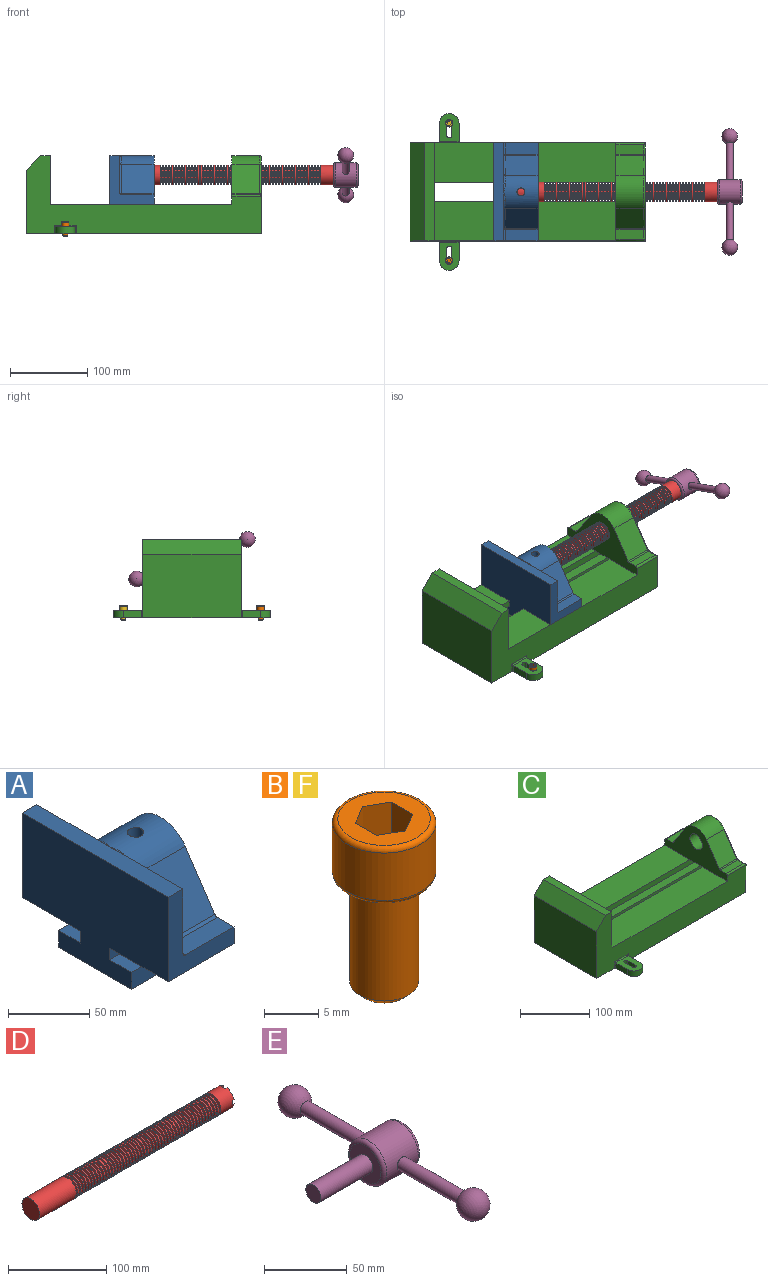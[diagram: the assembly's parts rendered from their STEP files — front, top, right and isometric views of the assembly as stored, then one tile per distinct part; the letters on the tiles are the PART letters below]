
ASSEMBLY  parts=6 mates=6
PART A: 36 faces, bbox 57.2x127x89 mm
  f0: plane 57.15x50.8mm, normal (0,0,-1), area 2903.2mm2, adj f6,f9,f10,f23
  f1: cylinder r=12.7mm len=44.45mm, axis (1,0,0), area 3464.3mm2, adj f6,f15,f16
  f2: plane 41.91x14.52mm, normal (0,0,1), area 608.5mm2, adj f6,f11,f24,f25
  f3: plane 51.86x48.26mm, normal (1,0,0), area 1495.7mm2, adj f8,f10,f31,f33,f35
  f4: plane 51.86x48.26mm, normal (1,0,0), area 1495.7mm2, adj f8,f11,f24,f28,f29
  f5: plane 57.15x50.8mm, normal (0,0,-1), area 2903.2mm2, adj f6,f9,f11,f22
  f6: plane 127x85.09mm, normal (1,0,0), area 5190.6mm2, adj f0,f1,f2,f5,f7,f10,f11,f12
  f7: plane 41.91x14.52mm, normal (0,0,1), area 608.5mm2, adj f6,f10,f30,f31
  f8: plane 127x12.7mm, normal (0,0,1), area 1612.9mm2, adj f3,f4,f9,f10,f11,f26,f34
  f9: plane 127x85.09mm, normal (-1,0,0), area 9096.8mm2, adj f0,f5,f8,f10,f11,f17,f18,f19
  f10: plane 63.5x57.15mm, normal (0,-1,0), area 1372.3mm2, adj f0,f3,f6,f7,f8,f9,f31
  f11: plane 63.5x57.15mm, normal (0,1,0), area 1372.3mm2, adj f2,f4,f5,f6,f8,f9,f24
  f12: plane 41.91x38.43mm, normal (0,-0.83,0.56), area 1939.2mm2, adj f6,f13,f30,f33
  f13: cylinder r=25.4mm len=44.45mm, axis (1,0,0), area 2026.5mm2, adj f6,f12,f14,f16,f26,f28,f34,f35
  f14: plane 41.91x38.43mm, normal (0,0.83,0.56), area 1939.2mm2, adj f6,f13,f25,f29
  f15: plane 25.4x25.4mm, normal (1,0,0), area 506.7mm2, adj f1
  f16: cylinder r=5.08mm len=13.76mm, axis (0,0,1), area 414mm2, adj f1,f13
  f17: plane 57.15x19.05mm, normal (0,0,1), area 1088.7mm2, adj f6,f9,f18,f23
  f18: plane 57.15x12.7mm, normal (0,-1,0), area 725.8mm2, adj f6,f9,f17,f19
  f19: plane 63.5x57.15mm, normal (0,0,-1), area 3629mm2, adj f6,f9,f18,f20
  f20: plane 57.15x12.7mm, normal (0,1,0), area 725.8mm2, adj f6,f9,f19,f21
  f21: plane 57.15x19.05mm, normal (0,0,1), area 1088.7mm2, adj f6,f9,f20,f22
  f22: plane 57.15x8.89mm, normal (0,1,0), area 508.1mm2, adj f5,f6,f9,f21
  f23: plane 57.15x8.89mm, normal (0,-1,0), area 508.1mm2, adj f0,f6,f9,f17
  f24: cylinder r=2.54mm len=14.52mm, axis (0,-1,0), area 57.9mm2, adj f2,f4,f11,f27
  f25: cylinder r=2.54mm len=41.91mm, axis (1,0,0), area 104.3mm2, adj f2,f6,f14,f27
  f26: bspline ~12.24x2.8mm, area 20.9mm2, adj f8,f13,f28
  f27: sphere r=2.54mm, area 6.3mm2, adj f24,f25,f29
  f28: torus R=27.94mm, axis (1,0,0), area 57.8mm2, adj f4,f13,f26,f29
  f29: cylinder r=2.54mm len=39.84mm, axis (0,-0.56,0.83), area 184.6mm2, adj f4,f14,f27,f28
  f30: cylinder r=2.54mm len=41.91mm, axis (1,0,0), area 104.3mm2, adj f6,f7,f12,f32
  f31: cylinder r=2.54mm len=14.52mm, axis (0,-1,0), area 57.9mm2, adj f3,f7,f10,f32
  f32: sphere r=2.54mm, area 6.3mm2, adj f30,f31,f33
  f33: cylinder r=2.54mm len=39.84mm, axis (0,-0.56,-0.83), area 184.6mm2, adj f3,f12,f32,f35
  f34: bspline ~12.24x2.8mm, area 20.9mm2, adj f8,f13,f35
  f35: torus R=27.94mm, axis (1,0,0), area 57.8mm2, adj f3,f13,f33,f34
PART B: 15 faces, bbox 10.3x10.3x19.1 mm
  f0: plane 8.51x8.51mm, normal (0,0,1), area 37.2mm2, adj f5,f6,f7,f8,f9,f10,f14
  f1: cylinder r=3.17mm len=11.94mm, axis (0,0,1), area 238.2mm2, adj f4,f12
  f2: plane 4.83x4.83mm, normal (0,0,-1), area 18.3mm2, adj f12
  f3: cylinder r=4.76mm len=9.53mm, axis (0,0,-1), area 159.6mm2, adj f13,f14
  f4: plane 8.51x8.51mm, normal (0,0,-1), area 25.2mm2, adj f1,f13
  f5: plane 4.83x2.38mm, normal (-0.5,-0.87,0), area 13.3mm2, adj f0,f6,f10,f11
  f6: plane 4.83x2.38mm, normal (0.5,-0.87,0), area 13.3mm2, adj f0,f5,f7,f11
  f7: plane 4.83x2.75mm, normal (1,0,0), area 13.3mm2, adj f0,f6,f8,f11
  f8: plane 4.83x2.38mm, normal (0.5,0.87,0), area 13.3mm2, adj f0,f7,f9,f11
  f9: plane 4.83x2.38mm, normal (-0.5,0.87,0), area 13.3mm2, adj f0,f8,f10,f11
  f10: plane 4.83x2.75mm, normal (-1,0,0), area 13.3mm2, adj f0,f5,f9,f11
  f11: plane 5.5x4.76mm, normal (0,0,1), area 19.6mm2, adj f5,f6,f7,f8,f9,f10
  f12: cone r=3.17mm half-angle=45deg, axis (0,0,1), area 18.9mm2, adj f1,f2
  f13: torus R=4.25mm, axis (0,0,1), area 23mm2, adj f3,f4
  f14: torus R=4.25mm, axis (0,0,1), area 23mm2, adj f0,f3
PART C: 61 faces, bbox 304.8x203.2x103.7 mm
  f0: plane 304.8x101.6mm, normal (0,1,0), area 13520.3mm2, adj f3,f4,f5,f6,f7,f8,f9,f16
  f1: plane 304.8x101.6mm, normal (0,-1,0), area 13520.3mm2, adj f2,f3,f5,f6,f7,f8,f9,f16
  f2: plane 234.95x50.8mm, normal (0,0,1), area 11935.5mm2, adj f1,f5,f16,f26
  f3: plane 127x99.06mm, normal (1,0,0), area 7097.5mm2, adj f0,f1,f9,f14,f17,f18,f19,f20
  f4: plane 234.95x50.8mm, normal (0,0,1), area 11935.5mm2, adj f0,f5,f16,f27
  f5: plane 127x101.6mm, normal (1,0,0), area 9516.1mm2, adj f0,f1,f2,f4,f6,f9,f18,f19
  f6: plane 127x12.7mm, normal (0,0,1), area 1612.9mm2, adj f0,f1,f5,f7
  f7: plane 127x19.05mm, normal (-0.71,0,0.71), area 3421.5mm2, adj f0,f1,f6,f8
  f8: plane 127x82.55mm, normal (-1,0,0), area 10483.8mm2, adj f0,f1,f7,f9
  f9: plane 304.8x203.2mm, normal (0,0,-1), area 33298.3mm2, adj f0,f1,f3,f5,f8,f21,f22,f39
  f10: plane 35.56x11.98mm, normal (0,0,1), area 426mm2, adj f16,f28,f29,f30
  f11: plane 38.43x35.56mm, normal (0,0.83,0.56), area 1645.4mm2, adj f12,f16,f29,f32
  f12: cylinder r=25.4mm len=42.19mm, axis (1,0,0), area 1770.2mm2, adj f11,f13,f16,f33
  f13: plane 38.43x35.56mm, normal (0,-0.83,0.56), area 1645.4mm2, adj f12,f16,f34,f35
  f14: cylinder r=12.7mm len=38.1mm, axis (1,0,0), area 3040.2mm2, adj f3,f16
  f15: plane 35.56x11.98mm, normal (0,0,1), area 426mm2, adj f16,f34,f36,f38
  f16: plane 127x63.5mm, normal (-1,0,0), area 4155.5mm2, adj f0,f1,f2,f4,f10,f11,f12,f13
  f17: plane 38.1x25.4mm, normal (0,0,-1), area 967.7mm2, adj f3,f16,f26,f27
  f18: plane 273.05x19.05mm, normal (0,0,-1), area 5201.6mm2, adj f3,f5,f19,f26
  f19: plane 273.05x12.7mm, normal (0,1,0), area 3467.7mm2, adj f3,f5,f18,f20
  f20: plane 273.05x19.05mm, normal (0,0,1), area 5201.6mm2, adj f3,f5,f19,f21
  f21: plane 273.05x16.51mm, normal (0,1,0), area 4508.1mm2, adj f3,f5,f9,f20
  f22: plane 273.05x16.51mm, normal (0,-1,0), area 4508.1mm2, adj f3,f5,f9,f23
  f23: plane 273.05x19.05mm, normal (0,0,1), area 5201.6mm2, adj f3,f5,f22,f24
  f24: plane 273.05x12.7mm, normal (0,-1,0), area 3467.7mm2, adj f3,f5,f23,f25
  f25: plane 273.05x19.05mm, normal (0,0,-1), area 5201.6mm2, adj f3,f5,f24,f27
  f26: plane 273.05x8.89mm, normal (0,1,0), area 2427.4mm2, adj f2,f3,f5,f17,f18
  f27: plane 273.05x8.89mm, normal (0,-1,0), area 2427.4mm2, adj f3,f4,f5,f17,f25
  f28: cylinder r=2.54mm len=38.1mm, axis (1,0,0), area 148.3mm2, adj f0,f10,f16,f30
  f29: cylinder r=2.54mm len=35.56mm, axis (-1,0,0), area 88.5mm2, adj f10,f11,f16,f31
  f30: cylinder r=2.54mm len=14.52mm, axis (0,1,0), area 54.3mm2, adj f3,f10,f28,f31
  f31: torus R=5.08mm, axis (-1,0,0), area 13.5mm2, adj f3,f29,f30,f32
  f32: cylinder r=2.54mm len=39.84mm, axis (0,0.56,-0.83), area 184.6mm2, adj f3,f11,f31,f33
  f33: torus R=22.86mm, axis (-1,0,0), area 191.4mm2, adj f3,f12,f32,f35
  f34: cylinder r=2.54mm len=35.56mm, axis (-1,0,0), area 88.5mm2, adj f13,f15,f16,f37
  f35: cylinder r=2.54mm len=39.84mm, axis (0,0.56,0.83), area 184.6mm2, adj f3,f13,f33,f37
  f36: cylinder r=2.54mm len=38.1mm, axis (-1,0,0), area 148.3mm2, adj f1,f15,f16,f38
  f37: torus R=5.08mm, axis (-1,0,0), area 13.5mm2, adj f3,f34,f35,f38
  f38: cylinder r=2.54mm len=14.52mm, axis (0,1,0), area 54.3mm2, adj f3,f15,f36,f37
  f39: plane 23.88x9.53mm, normal (-1,0,0), area 227.4mm2, adj f9,f45,f46,f60
  f40: plane 23.88x9.53mm, normal (1,0,0), area 227.4mm2, adj f9,f45,f46,f58
  f41: cylinder r=3.3mm len=9.53mm, axis (0,0,-1), area 98.8mm2, adj f9,f42,f44,f46
  f42: plane 15.62x9.53mm, normal (-1,0,0), area 148.8mm2, adj f9,f41,f43,f46
  f43: cylinder r=3.3mm len=9.53mm, axis (0,0,-1), area 98.8mm2, adj f9,f42,f44,f46
  f44: plane 15.62x9.53mm, normal (1,0,0), area 148.8mm2, adj f9,f41,f43,f46
  f45: cylinder r=12.7mm len=25.4mm, axis (0,0,-1), area 380mm2, adj f9,f39,f40,f46
  f46: plane 36.58x25.4mm, normal (0,0,1), area 722.4mm2, adj f39,f40,f41,f42,f43,f44,f45,f59
  f47: plane 23.88x9.53mm, normal (-1,0,0), area 227.4mm2, adj f9,f53,f54,f56
  f48: plane 23.88x9.53mm, normal (1,0,0), area 227.4mm2, adj f9,f53,f54,f55
  f49: cylinder r=3.3mm len=9.53mm, axis (0,0,-1), area 98.8mm2, adj f9,f50,f52,f54
  f50: plane 15.62x9.53mm, normal (-1,0,0), area 148.8mm2, adj f9,f49,f51,f54
  f51: cylinder r=3.3mm len=9.53mm, axis (0,0,-1), area 98.8mm2, adj f9,f50,f52,f54
  f52: plane 15.62x9.53mm, normal (1,0,0), area 148.8mm2, adj f9,f49,f51,f54
  f53: cylinder r=12.7mm len=25.4mm, axis (0,0,-1), area 380mm2, adj f9,f47,f48,f54
  f54: plane 36.58x25.4mm, normal (0,0,1), area 722.4mm2, adj f47,f48,f49,f50,f51,f52,f53,f57
  f55: cylinder r=1.52mm len=11.05mm, axis (0,0,-1), area 24.1mm2, adj f0,f9,f48,f57
  f56: cylinder r=1.52mm len=11.05mm, axis (0,0,1), area 24.1mm2, adj f0,f9,f47,f57
  f57: cylinder r=1.52mm len=28.45mm, axis (1,0,0), area 63.5mm2, adj f0,f54,f55,f56
  f58: cylinder r=1.52mm len=11.05mm, axis (0,0,1), area 24.1mm2, adj f1,f9,f40,f59
  f59: cylinder r=1.52mm len=28.45mm, axis (-1,0,0), area 63.5mm2, adj f1,f46,f58,f60
  f60: cylinder r=1.52mm len=11.05mm, axis (0,0,-1), area 24.1mm2, adj f1,f9,f39,f59
PART D: 220 faces, bbox 279.4x25.4x25.4 mm
  f0: cylinder r=12.7mm len=25.4mm, axis (-1,0,0), area 1468.2mm2, adj f1,f2,f3,f5,f7,f208,f209,f210
  f1: plane 9.9x9.9mm, normal (1,0,0), area 62.3mm2, adj f0,f4,f213,f216
  f2: plane 9.9x9.9mm, normal (1,0,0), area 62.3mm2, adj f0,f4,f210,f218
  f3: plane 9.9x9.9mm, normal (1,0,0), area 62.3mm2, adj f0,f4,f209,f212
  f4: cylinder r=6.35mm len=25.4mm, axis (1,0,0), area 960.3mm2, adj f1,f2,f3,f5,f6,f208,f209,f210
  f5: plane 9.9x9.9mm, normal (1,0,0), area 62.3mm2, adj f0,f4,f215,f217
  f6: plane 12.7x12.7mm, normal (1,0,0), area 126.7mm2, adj f4
  f7: cone r=12.7mm half-angle=76deg, axis (1,0,0), area 188mm2, adj f0,f9
  f8: cone r=10.16mm half-angle=76deg, axis (-1,0,0), area 188mm2, adj f9,f10
  f9: cylinder r=10.16mm len=20.32mm, axis (1,0,0), area 81.1mm2, adj f7,f8
  f10: cylinder r=12.7mm len=25.4mm, axis (-1,0,0), area 131.7mm2, adj f8,f11
  f11: cone r=12.7mm half-angle=76deg, axis (1,0,0), area 188mm2, adj f10,f13
  f12: cone r=10.16mm half-angle=76deg, axis (-1,0,0), area 188mm2, adj f13,f14
  f13: cylinder r=10.16mm len=20.32mm, axis (1,0,0), area 81.1mm2, adj f11,f12
  f14: cylinder r=12.7mm len=25.4mm, axis (-1,0,0), area 131.7mm2, adj f12,f15
  f15: cone r=12.7mm half-angle=76deg, axis (1,0,0), area 188mm2, adj f14,f17
  f16: cone r=10.16mm half-angle=76deg, axis (-1,0,0), area 188mm2, adj f17,f18
  f17: cylinder r=10.16mm len=20.32mm, axis (1,0,0), area 81.1mm2, adj f15,f16
  f18: cylinder r=12.7mm len=25.4mm, axis (-1,0,0), area 131.7mm2, adj f16,f19
  f19: cone r=12.7mm half-angle=76deg, axis (1,0,0), area 188mm2, adj f18,f21
  f20: cone r=10.16mm half-angle=76deg, axis (-1,0,0), area 188mm2, adj f21,f22
  f21: cylinder r=10.16mm len=20.32mm, axis (1,0,0), area 81.1mm2, adj f19,f20
  f22: cylinder r=12.7mm len=25.4mm, axis (-1,0,0), area 131.7mm2, adj f20,f23
  f23: cone r=12.7mm half-angle=76deg, axis (1,0,0), area 188mm2, adj f22,f25
  f24: cone r=10.16mm half-angle=76deg, axis (-1,0,0), area 188mm2, adj f25,f26
  f25: cylinder r=10.16mm len=20.32mm, axis (1,0,0), area 81.1mm2, adj f23,f24
  f26: cylinder r=12.7mm len=25.4mm, axis (-1,0,0), area 131.7mm2, adj f24,f27
  f27: cone r=12.7mm half-angle=76deg, axis (1,0,0), area 188mm2, adj f26,f29
  f28: cone r=10.16mm half-angle=76deg, axis (-1,0,0), area 188mm2, adj f29,f30
  f29: cylinder r=10.16mm len=20.32mm, axis (1,0,0), area 81.1mm2, adj f27,f28
  f30: cylinder r=12.7mm len=25.4mm, axis (-1,0,0), area 131.7mm2, adj f28,f31
  f31: cone r=12.7mm half-angle=76deg, axis (1,0,0), area 188mm2, adj f30,f33
  f32: cone r=10.16mm half-angle=76deg, axis (-1,0,0), area 188mm2, adj f33,f34
  f33: cylinder r=10.16mm len=20.32mm, axis (1,0,0), area 81.1mm2, adj f31,f32
  f34: cylinder r=12.7mm len=25.4mm, axis (-1,0,0), area 131.7mm2, adj f32,f35
  f35: cone r=12.7mm half-angle=76deg, axis (1,0,0), area 188mm2, adj f34,f37
  f36: cone r=10.16mm half-angle=76deg, axis (-1,0,0), area 188mm2, adj f37,f38
  f37: cylinder r=10.16mm len=20.32mm, axis (1,0,0), area 81.1mm2, adj f35,f36
  f38: cylinder r=12.7mm len=25.4mm, axis (-1,0,0), area 131.7mm2, adj f36,f39
  f39: cone r=12.7mm half-angle=76deg, axis (1,0,0), area 188mm2, adj f38,f41
  f40: cone r=10.16mm half-angle=76deg, axis (-1,0,0), area 188mm2, adj f41,f42
  f41: cylinder r=10.16mm len=20.32mm, axis (1,0,0), area 81.1mm2, adj f39,f40
  f42: cylinder r=12.7mm len=25.4mm, axis (-1,0,0), area 131.7mm2, adj f40,f43
  f43: cone r=12.7mm half-angle=76deg, axis (1,0,0), area 188mm2, adj f42,f45
  f44: cone r=10.16mm half-angle=76deg, axis (-1,0,0), area 188mm2, adj f45,f46
  f45: cylinder r=10.16mm len=20.32mm, axis (1,0,0), area 81.1mm2, adj f43,f44
  f46: cylinder r=12.7mm len=25.4mm, axis (-1,0,0), area 131.7mm2, adj f44,f47
  f47: cone r=12.7mm half-angle=76deg, axis (1,0,0), area 188mm2, adj f46,f49
  f48: cone r=10.16mm half-angle=76deg, axis (-1,0,0), area 188mm2, adj f49,f50
  f49: cylinder r=10.16mm len=20.32mm, axis (1,0,0), area 81.1mm2, adj f47,f48
  f50: cylinder r=12.7mm len=25.4mm, axis (-1,0,0), area 131.7mm2, adj f48,f51
  f51: cone r=12.7mm half-angle=76deg, axis (1,0,0), area 188mm2, adj f50,f53
  f52: cone r=10.16mm half-angle=76deg, axis (-1,0,0), area 188mm2, adj f53,f54
  f53: cylinder r=10.16mm len=20.32mm, axis (1,0,0), area 81.1mm2, adj f51,f52
  f54: cylinder r=12.7mm len=25.4mm, axis (-1,0,0), area 131.7mm2, adj f52,f55
  f55: cone r=12.7mm half-angle=76deg, axis (1,0,0), area 188mm2, adj f54,f57
  f56: cone r=10.16mm half-angle=76deg, axis (-1,0,0), area 188mm2, adj f57,f58
  f57: cylinder r=10.16mm len=20.32mm, axis (1,0,0), area 81.1mm2, adj f55,f56
  f58: cylinder r=12.7mm len=25.4mm, axis (-1,0,0), area 131.7mm2, adj f56,f59
  f59: cone r=12.7mm half-angle=76deg, axis (1,0,0), area 188mm2, adj f58,f61
  f60: cone r=10.16mm half-angle=76deg, axis (-1,0,0), area 188mm2, adj f61,f62
  f61: cylinder r=10.16mm len=20.32mm, axis (1,0,0), area 81.1mm2, adj f59,f60
  f62: cylinder r=12.7mm len=25.4mm, axis (-1,0,0), area 131.7mm2, adj f60,f63
  f63: cone r=12.7mm half-angle=76deg, axis (1,0,0), area 188mm2, adj f62,f65
  f64: cone r=10.16mm half-angle=76deg, axis (-1,0,0), area 188mm2, adj f65,f66
  f65: cylinder r=10.16mm len=20.32mm, axis (1,0,0), area 81.1mm2, adj f63,f64
  f66: cylinder r=12.7mm len=25.4mm, axis (-1,0,0), area 131.7mm2, adj f64,f67
  f67: cone r=12.7mm half-angle=76deg, axis (1,0,0), area 188mm2, adj f66,f69
  f68: cone r=10.16mm half-angle=76deg, axis (-1,0,0), area 188mm2, adj f69,f70
  f69: cylinder r=10.16mm len=20.32mm, axis (1,0,0), area 81.1mm2, adj f67,f68
  f70: cylinder r=12.7mm len=25.4mm, axis (-1,0,0), area 131.7mm2, adj f68,f71
  f71: cone r=12.7mm half-angle=76deg, axis (1,0,0), area 188mm2, adj f70,f73
  f72: cone r=10.16mm half-angle=76deg, axis (-1,0,0), area 188mm2, adj f73,f74
  f73: cylinder r=10.16mm len=20.32mm, axis (1,0,0), area 81.1mm2, adj f71,f72
  f74: cylinder r=12.7mm len=25.4mm, axis (-1,0,0), area 131.7mm2, adj f72,f75
  f75: cone r=12.7mm half-angle=76deg, axis (1,0,0), area 188mm2, adj f74,f77
  f76: cone r=10.16mm half-angle=76deg, axis (-1,0,0), area 188mm2, adj f77,f78
  f77: cylinder r=10.16mm len=20.32mm, axis (1,0,0), area 81.1mm2, adj f75,f76
  f78: cylinder r=12.7mm len=25.4mm, axis (-1,0,0), area 131.7mm2, adj f76,f79
  f79: cone r=12.7mm half-angle=76deg, axis (1,0,0), area 188mm2, adj f78,f81
  f80: cone r=10.16mm half-angle=76deg, axis (-1,0,0), area 188mm2, adj f81,f82
  f81: cylinder r=10.16mm len=20.32mm, axis (1,0,0), area 81.1mm2, adj f79,f80
  f82: cylinder r=12.7mm len=25.4mm, axis (-1,0,0), area 131.7mm2, adj f80,f83
  f83: cone r=12.7mm half-angle=76deg, axis (1,0,0), area 188mm2, adj f82,f85
  f84: cone r=10.16mm half-angle=76deg, axis (-1,0,0), area 188mm2, adj f85,f86
  f85: cylinder r=10.16mm len=20.32mm, axis (1,0,0), area 81.1mm2, adj f83,f84
  f86: cylinder r=12.7mm len=25.4mm, axis (-1,0,0), area 131.7mm2, adj f84,f87
  f87: cone r=12.7mm half-angle=76deg, axis (1,0,0), area 188mm2, adj f86,f89
  f88: cone r=10.16mm half-angle=76deg, axis (-1,0,0), area 188mm2, adj f89,f90
  f89: cylinder r=10.16mm len=20.32mm, axis (1,0,0), area 81.1mm2, adj f87,f88
  f90: cylinder r=12.7mm len=25.4mm, axis (-1,0,0), area 131.7mm2, adj f88,f91
  f91: cone r=12.7mm half-angle=76deg, axis (1,0,0), area 188mm2, adj f90,f93
  f92: cone r=10.16mm half-angle=76deg, axis (-1,0,0), area 188mm2, adj f93,f94
  f93: cylinder r=10.16mm len=20.32mm, axis (1,0,0), area 81.1mm2, adj f91,f92
  f94: cylinder r=12.7mm len=25.4mm, axis (-1,0,0), area 131.7mm2, adj f92,f95
  f95: cone r=12.7mm half-angle=76deg, axis (1,0,0), area 188mm2, adj f94,f97
  f96: cone r=10.16mm half-angle=76deg, axis (-1,0,0), area 188mm2, adj f97,f98
  f97: cylinder r=10.16mm len=20.32mm, axis (1,0,0), area 81.1mm2, adj f95,f96
  f98: cylinder r=12.7mm len=25.4mm, axis (-1,0,0), area 131.7mm2, adj f96,f99
  f99: cone r=12.7mm half-angle=76deg, axis (1,0,0), area 188mm2, adj f98,f101
  f100: cone r=10.16mm half-angle=76deg, axis (-1,0,0), area 188mm2, adj f101,f102
  f101: cylinder r=10.16mm len=20.32mm, axis (1,0,0), area 81.1mm2, adj f99,f100
  f102: cylinder r=12.7mm len=25.4mm, axis (-1,0,0), area 131.7mm2, adj f100,f103
  f103: cone r=12.7mm half-angle=76deg, axis (1,0,0), area 188mm2, adj f102,f105
  f104: cone r=10.16mm half-angle=76deg, axis (-1,0,0), area 188mm2, adj f105,f106
  f105: cylinder r=10.16mm len=20.32mm, axis (1,0,0), area 81.1mm2, adj f103,f104
  f106: cylinder r=12.7mm len=25.4mm, axis (-1,0,0), area 131.7mm2, adj f104,f107
  f107: cone r=12.7mm half-angle=76deg, axis (1,0,0), area 188mm2, adj f106,f109
  f108: cone r=10.16mm half-angle=76deg, axis (-1,0,0), area 188mm2, adj f109,f110
  f109: cylinder r=10.16mm len=20.32mm, axis (1,0,0), area 81.1mm2, adj f107,f108
  f110: cylinder r=12.7mm len=25.4mm, axis (-1,0,0), area 131.7mm2, adj f108,f111
  f111: cone r=12.7mm half-angle=76deg, axis (1,0,0), area 188mm2, adj f110,f113
  f112: cone r=10.16mm half-angle=76deg, axis (-1,0,0), area 188mm2, adj f113,f114
  f113: cylinder r=10.16mm len=20.32mm, axis (1,0,0), area 81.1mm2, adj f111,f112
  f114: cylinder r=12.7mm len=25.4mm, axis (-1,0,0), area 131.7mm2, adj f112,f115
  f115: cone r=12.7mm half-angle=76deg, axis (1,0,0), area 188mm2, adj f114,f117
  f116: cone r=10.16mm half-angle=76deg, axis (-1,0,0), area 188mm2, adj f117,f118
  f117: cylinder r=10.16mm len=20.32mm, axis (1,0,0), area 81.1mm2, adj f115,f116
  f118: cylinder r=12.7mm len=25.4mm, axis (-1,0,0), area 131.7mm2, adj f116,f119
  f119: cone r=12.7mm half-angle=76deg, axis (1,0,0), area 188mm2, adj f118,f121
  f120: cone r=10.16mm half-angle=76deg, axis (-1,0,0), area 188mm2, adj f121,f122
  f121: cylinder r=10.16mm len=20.32mm, axis (1,0,0), area 81.1mm2, adj f119,f120
  f122: cylinder r=12.7mm len=25.4mm, axis (-1,0,0), area 131.7mm2, adj f120,f123
  f123: cone r=12.7mm half-angle=76deg, axis (1,0,0), area 188mm2, adj f122,f125
  f124: cone r=10.16mm half-angle=76deg, axis (-1,0,0), area 188mm2, adj f125,f126
  f125: cylinder r=10.16mm len=20.32mm, axis (1,0,0), area 81.1mm2, adj f123,f124
  f126: cylinder r=12.7mm len=25.4mm, axis (-1,0,0), area 131.7mm2, adj f124,f127
  f127: cone r=12.7mm half-angle=76deg, axis (1,0,0), area 188mm2, adj f126,f129
  f128: cone r=10.16mm half-angle=76deg, axis (-1,0,0), area 188mm2, adj f129,f130
  f129: cylinder r=10.16mm len=20.32mm, axis (1,0,0), area 81.1mm2, adj f127,f128
  f130: cylinder r=12.7mm len=25.4mm, axis (-1,0,0), area 131.7mm2, adj f128,f131
  f131: cone r=12.7mm half-angle=76deg, axis (1,0,0), area 188mm2, adj f130,f133
  f132: cone r=10.16mm half-angle=76deg, axis (-1,0,0), area 188mm2, adj f133,f134
  f133: cylinder r=10.16mm len=20.32mm, axis (1,0,0), area 81.1mm2, adj f131,f132
  f134: cylinder r=12.7mm len=25.4mm, axis (-1,0,0), area 131.7mm2, adj f132,f135
  f135: cone r=12.7mm half-angle=76deg, axis (1,0,0), area 188mm2, adj f134,f137
  f136: cone r=10.16mm half-angle=76deg, axis (-1,0,0), area 188mm2, adj f137,f138
  f137: cylinder r=10.16mm len=20.32mm, axis (1,0,0), area 81.1mm2, adj f135,f136
  f138: cylinder r=12.7mm len=25.4mm, axis (-1,0,0), area 131.7mm2, adj f136,f139
  f139: cone r=12.7mm half-angle=76deg, axis (1,0,0), area 188mm2, adj f138,f141
  f140: cone r=10.16mm half-angle=76deg, axis (-1,0,0), area 188mm2, adj f141,f142
  f141: cylinder r=10.16mm len=20.32mm, axis (1,0,0), area 81.1mm2, adj f139,f140
  f142: cylinder r=12.7mm len=25.4mm, axis (-1,0,0), area 131.7mm2, adj f140,f143
  f143: cone r=12.7mm half-angle=76deg, axis (1,0,0), area 188mm2, adj f142,f145
  f144: cone r=10.16mm half-angle=76deg, axis (-1,0,0), area 188mm2, adj f145,f146
  f145: cylinder r=10.16mm len=20.32mm, axis (1,0,0), area 81.1mm2, adj f143,f144
  f146: cylinder r=12.7mm len=25.4mm, axis (-1,0,0), area 131.7mm2, adj f144,f147
  f147: cone r=12.7mm half-angle=76deg, axis (1,0,0), area 188mm2, adj f146,f149
  f148: cone r=10.16mm half-angle=76deg, axis (-1,0,0), area 188mm2, adj f149,f150
  f149: cylinder r=10.16mm len=20.32mm, axis (1,0,0), area 81.1mm2, adj f147,f148
  f150: cylinder r=12.7mm len=25.4mm, axis (-1,0,0), area 131.7mm2, adj f148,f151
  f151: cone r=12.7mm half-angle=76deg, axis (1,0,0), area 188mm2, adj f150,f153
  f152: cone r=10.16mm half-angle=76deg, axis (-1,0,0), area 188mm2, adj f153,f154
  f153: cylinder r=10.16mm len=20.32mm, axis (1,0,0), area 81.1mm2, adj f151,f152
  f154: cylinder r=12.7mm len=25.4mm, axis (-1,0,0), area 131.7mm2, adj f152,f155
  f155: cone r=12.7mm half-angle=76deg, axis (1,0,0), area 188mm2, adj f154,f157
  f156: cone r=10.16mm half-angle=76deg, axis (-1,0,0), area 188mm2, adj f157,f158
  f157: cylinder r=10.16mm len=20.32mm, axis (1,0,0), area 81.1mm2, adj f155,f156
  f158: cylinder r=12.7mm len=25.4mm, axis (-1,0,0), area 131.7mm2, adj f156,f159
  f159: cone r=12.7mm half-angle=76deg, axis (1,0,0), area 188mm2, adj f158,f161
  f160: cone r=10.16mm half-angle=76deg, axis (-1,0,0), area 188mm2, adj f161,f162
  f161: cylinder r=10.16mm len=20.32mm, axis (1,0,0), area 81.1mm2, adj f159,f160
  f162: cylinder r=12.7mm len=25.4mm, axis (-1,0,0), area 131.7mm2, adj f160,f163
  f163: cone r=12.7mm half-angle=76deg, axis (1,0,0), area 188mm2, adj f162,f165
  f164: cone r=10.16mm half-angle=76deg, axis (-1,0,0), area 188mm2, adj f165,f166
  f165: cylinder r=10.16mm len=20.32mm, axis (1,0,0), area 81.1mm2, adj f163,f164
  f166: cylinder r=12.7mm len=25.4mm, axis (-1,0,0), area 131.7mm2, adj f164,f167
  f167: cone r=12.7mm half-angle=76deg, axis (1,0,0), area 188mm2, adj f166,f169
  f168: cone r=10.16mm half-angle=76deg, axis (-1,0,0), area 188mm2, adj f169,f170
  f169: cylinder r=10.16mm len=20.32mm, axis (1,0,0), area 81.1mm2, adj f167,f168
  f170: cylinder r=12.7mm len=25.4mm, axis (-1,0,0), area 131.7mm2, adj f168,f171
  f171: cone r=12.7mm half-angle=76deg, axis (1,0,0), area 188mm2, adj f170,f173
  f172: cone r=10.16mm half-angle=76deg, axis (-1,0,0), area 188mm2, adj f173,f174
  f173: cylinder r=10.16mm len=20.32mm, axis (1,0,0), area 81.1mm2, adj f171,f172
  f174: cylinder r=12.7mm len=25.4mm, axis (-1,0,0), area 131.7mm2, adj f172,f175
  f175: cone r=12.7mm half-angle=76deg, axis (1,0,0), area 188mm2, adj f174,f177
  f176: cone r=10.16mm half-angle=76deg, axis (-1,0,0), area 188mm2, adj f177,f178
  f177: cylinder r=10.16mm len=20.32mm, axis (1,0,0), area 81.1mm2, adj f175,f176
  f178: cylinder r=12.7mm len=25.4mm, axis (-1,0,0), area 131.7mm2, adj f176,f179
  f179: cone r=12.7mm half-angle=76deg, axis (1,0,0), area 188mm2, adj f178,f181
  f180: cone r=10.16mm half-angle=76deg, axis (-1,0,0), area 188mm2, adj f181,f182
  f181: cylinder r=10.16mm len=20.32mm, axis (1,0,0), area 81.1mm2, adj f179,f180
  f182: cylinder r=12.7mm len=25.4mm, axis (-1,0,0), area 131.7mm2, adj f180,f183
  f183: cone r=12.7mm half-angle=76deg, axis (1,0,0), area 188mm2, adj f182,f185
  f184: cone r=10.16mm half-angle=76deg, axis (-1,0,0), area 188mm2, adj f185,f186
  f185: cylinder r=10.16mm len=20.32mm, axis (1,0,0), area 81.1mm2, adj f183,f184
  f186: cylinder r=12.7mm len=25.4mm, axis (-1,0,0), area 131.7mm2, adj f184,f187
  f187: cone r=12.7mm half-angle=76deg, axis (1,0,0), area 188mm2, adj f186,f189
  f188: cone r=10.16mm half-angle=76deg, axis (-1,0,0), area 188mm2, adj f189,f190
  f189: cylinder r=10.16mm len=20.32mm, axis (1,0,0), area 81.1mm2, adj f187,f188
  f190: cylinder r=12.7mm len=25.4mm, axis (-1,0,0), area 131.7mm2, adj f188,f191
  f191: cone r=12.7mm half-angle=76deg, axis (1,0,0), area 188mm2, adj f190,f193
  f192: cone r=10.16mm half-angle=76deg, axis (-1,0,0), area 188mm2, adj f193,f194
  f193: cylinder r=10.16mm len=20.32mm, axis (1,0,0), area 81.1mm2, adj f191,f192
  f194: cylinder r=12.7mm len=25.4mm, axis (-1,0,0), area 131.7mm2, adj f192,f195
  f195: cone r=12.7mm half-angle=76deg, axis (1,0,0), area 188mm2, adj f194,f197
  f196: cone r=10.16mm half-angle=76deg, axis (-1,0,0), area 188mm2, adj f197,f198
  f197: cylinder r=10.16mm len=20.32mm, axis (1,0,0), area 81.1mm2, adj f195,f196
  f198: cylinder r=12.7mm len=25.4mm, axis (-1,0,0), area 131.7mm2, adj f196,f199
  f199: cone r=12.7mm half-angle=76deg, axis (1,0,0), area 188mm2, adj f198,f201
  f200: cone r=10.16mm half-angle=76deg, axis (-1,0,0), area 188mm2, adj f201,f202
  f201: cylinder r=10.16mm len=20.32mm, axis (1,0,0), area 81.1mm2, adj f199,f200
  f202: cylinder r=12.7mm len=25.4mm, axis (-1,0,0), area 131.7mm2, adj f200,f203
  f203: cone r=12.7mm half-angle=76deg, axis (1,0,0), area 188mm2, adj f202,f205
  f204: cone r=10.16mm half-angle=76deg, axis (-1,0,0), area 188mm2, adj f205,f207
  f205: cylinder r=10.16mm len=20.32mm, axis (1,0,0), area 81.1mm2, adj f203,f204
  f206: plane 25.4x25.4mm, normal (-1,0,0), area 506.7mm2, adj f207
  f207: cylinder r=12.7mm len=52.45mm, axis (-1,0,0), area 4185.4mm2, adj f204,f206
  f208: plane 6.88x5.08mm, normal (1,0,0), area 32.7mm2, adj f0,f4,f209,f210
  f209: plane 6.62x2.54mm, normal (0,-1,0), area 16.8mm2, adj f0,f3,f4,f208
  f210: plane 6.62x2.54mm, normal (0,1,0), area 16.8mm2, adj f0,f2,f4,f208
  f211: plane 6.88x5.08mm, normal (1,0,0), area 32.7mm2, adj f0,f4,f212,f213
  f212: plane 6.62x2.54mm, normal (0,0,1), area 16.8mm2, adj f0,f3,f4,f211
  f213: plane 6.62x2.54mm, normal (0,0,-1), area 16.8mm2, adj f0,f1,f4,f211
  f214: plane 6.88x5.08mm, normal (1,0,0), area 32.7mm2, adj f0,f4,f215,f216
  f215: plane 6.62x2.54mm, normal (0,1,0), area 16.8mm2, adj f0,f4,f5,f214
  f216: plane 6.62x2.54mm, normal (0,-1,0), area 16.8mm2, adj f0,f1,f4,f214
  f217: plane 6.62x2.54mm, normal (0,0,-1), area 16.8mm2, adj f0,f4,f5,f219
  f218: plane 6.62x2.54mm, normal (0,0,1), area 16.8mm2, adj f0,f2,f4,f219
  f219: plane 6.88x5.08mm, normal (1,0,0), area 32.7mm2, adj f0,f4,f217,f218
PART E: 11 faces, bbox 76.2x172.7x34.4 mm
  f0: sphere r=10.16mm, area 1231.8mm2, adj f1
  f1: cylinder r=4.45mm len=51.82mm, axis (0,1,0), area 1438.5mm2, adj f0,f4
  f2: sphere r=10.16mm, area 1231.8mm2, adj f3
  f3: cylinder r=4.45mm len=51.82mm, axis (0,1,0), area 1438.5mm2, adj f2,f4
  f4: cylinder r=15.88mm len=31.75mm, axis (-1,0,0), area 2534.7mm2, adj f1,f3,f9,f10
  f5: cylinder r=6.35mm len=44.45mm, axis (-1,0,0), area 1773.5mm2, adj f6,f8
  f6: plane 12.7x12.7mm, normal (-1,0,0), area 126.7mm2, adj f5
  f7: plane 26.67x26.67mm, normal (1,0,0), area 558.6mm2, adj f10
  f8: plane 26.67x26.67mm, normal (-1,0,0), area 432mm2, adj f5,f9
  f9: torus R=13.33mm, axis (1,0,0), area 374.8mm2, adj f4,f8
  f10: torus R=13.33mm, axis (1,0,0), area 374.8mm2, adj f4,f7
PART F: same geometry as B
PLACE A t=(76.89,0,0)mm
PLACE B rot(axis=(0,0,1),17.4deg) t=(-254,-88.9,9.52)mm
PLACE C at identity fixed
PLACE D rot(axis=(1,0,0),160.4deg) t=(76.89,25.57,147.98)mm
PLACE E rot(axis=(1,0,0),160.4deg) t=(55.3,25.57,147.98)mm
PLACE F rot(axis=(0,0,1),48deg) t=(-254,88.9,9.53)mm
MATE fastened D.f4 <-> E.f5  axis (1,0,0) through (93.4,0,76.2)mm
MATE planar A.f0 <-> C.f2  axis (0,0,-1) through (-167.58,-38.1,38.1)mm
MATE pin_slot B.f1 <-> C.f41  axis (0,0,1) through (-254,-88.9,9.52)mm
MATE revolute D.f7 <-> A.f28  axis (-1,0,0) through (-183.46,0,76.2)mm
MATE pin_slot F.f1 <-> C.f49  axis (0,0,1) through (-254,88.9,9.52)mm
MATE cylindrical C.f12 <-> D.f7  axis (-1,0,0) through (-38.1,0,76.2)mm
